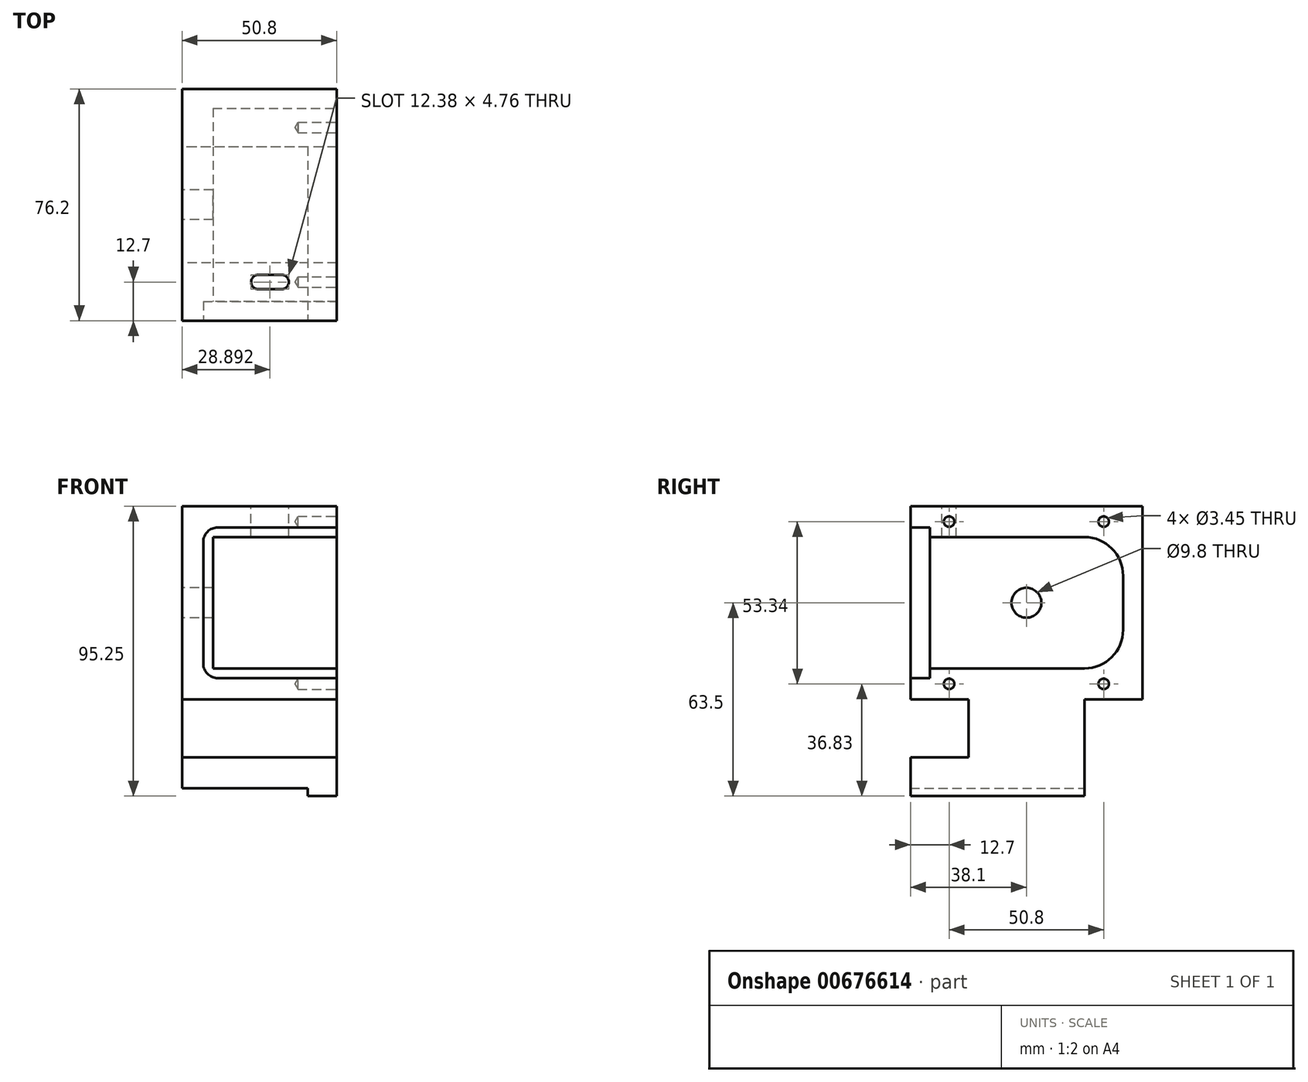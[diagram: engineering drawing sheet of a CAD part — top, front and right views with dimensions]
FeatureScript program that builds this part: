
annotation { "Feature Type Name" : "Feature", "Feature Type Description" : "" }
export const myFeature = defineFeature(function(context is Context, id is Id, definition is map)
    precondition{}
    {
        {
            var Q0;
            Q0=qCreatedBy(makeId("Right.planeOp"),FACE);
            var sketch = newSketch(context, id + "F0", { "sketchPlane" : qUnion([Q0])});
            skLineSegment(sketch, "E0.bottom", {"start": v(0, 0) * mm, "end": v(76.2, 0) * mm});
            skLineSegment(sketch, "E0.top", {"start": v(0, 63.5) * mm, "end": v(76.2, 63.5) * mm});
            skLineSegment(sketch, "E0.left", {"start": v(0, 0) * mm, "end": v(0, 63.5) * mm});
            skLineSegment(sketch, "E0.right", {"start": v(76.2, 0) * mm, "end": v(76.2, 63.5) * mm});
            skLineSegment(sketch, "E1.bottom", {"start": v(19.05, 0) * mm, "end": v(57.15, 0) * mm});
            skLineSegment(sketch, "E1.top", {"start": v(19.05, -19.05) * mm, "end": v(57.15, -19.05) * mm});
            skLineSegment(sketch, "E1.left", {"start": v(19.05, 0) * mm, "end": v(19.05, -19.05) * mm});
            skLineSegment(sketch, "E1.right", {"start": v(57.15, 0) * mm, "end": v(57.15, -19.05) * mm});
            skSolve(sketch);
        }
        {
            var Q0;
            Q0=qSketchRegion(id+"F0",true);
            extrude(context, id + "F1", {"entities" : qUnion([Q0]), "depth" : 50.8 * mm});
        }
        {
            var Q0;
            Q0=makeQuery(id+"F1.opExtrude","CAP_FACE",FACE,{"disambiguationData":[OSD([sQuery(id+"F0.wireOp",EDGE,"E0.bottom"),sQuery(id+"F0.wireOp",EDGE,"E0.top"),sQuery(id+"F0.wireOp",EDGE,"E0.left"),sQuery(id+"F0.wireOp",EDGE,"E0.right"),sQuery(id+"F0.wireOp",EDGE,"E1.top"),sQuery(id+"F0.wireOp",EDGE,"E1.left"),sQuery(id+"F0.wireOp",EDGE,"E1.right")])],"isStart":true});
            var sketch = newSketch(context, id + "F2", { "sketchPlane" : qUnion([Q0])});
            skCircle(sketch, "E2", {"center": v(-38.1, 31.75) * mm, "radius": 11.22 * mm});
            skSolve(sketch);
        }
        {
            var Q0;
            Q0=sQuery(id+"F2.wireOp",VERTEX,"E2.center");
            var Q1;
            Q1=makeQuery(id+"F1.opExtrude","SWEPT_BODY",BODY,{"disambiguationData":[OSD([sQuery(id+"F0.wireOp",EDGE,"E0.bottom"),sQuery(id+"F0.wireOp",EDGE,"E0.top"),sQuery(id+"F0.wireOp",EDGE,"E0.left"),sQuery(id+"F0.wireOp",EDGE,"E0.right"),sQuery(id+"F0.wireOp",EDGE,"E1.top"),sQuery(id+"F0.wireOp",EDGE,"E1.left"),sQuery(id+"F0.wireOp",EDGE,"E1.right")])]});
            hole(context, id + "F3", {"style" : HoleStyle.SIMPLE, "endStyle" : HoleEndStyle.THROUGH, "standardTappedOrClearance" : lookupTablePath({ "standard" : "ANSI", "fit" : "Close", "size" : "3/8", "type" : "Clearance" }), "standardBlindInLast" : lookupTablePath({ "fit" : "Close", "standard" : "ANSI", "size" : "3/8", "type" : "Clearance" }), "holeDiameter" : 9.8 * mm, "isTappedThrough" : true, "tappedDepth" : 3.96 * mm, "tapClearance" : 3, "locations" : qUnion([Q0]), "scope" : qUnion([Q1])});
        }
        {
            var Q0;
            Q0=makeQuery(id+"F1.opExtrude","SWEPT_FACE",FACE,{"disambiguationData":[OSD([sQuery(id+"F0.wireOp",EDGE,"E1.top")])]});
            var sketch = newSketch(context, id + "F4", { "sketchPlane" : qUnion([Q0])});
            skLineSegment(sketch, "E3.0", {"start": v(50.8, -76.2) * mm, "end": v(0, -76.2) * mm});
            skLineSegment(sketch, "E4.0", {"start": v(50.8, -57.15) * mm, "end": v(50.8, -76.2) * mm});
            skLineSegment(sketch, "E5.0", {"start": v(50.8, -19.05) * mm, "end": v(50.8, -57.15) * mm});
            skLineSegment(sketch, "E6.0", {"start": v(50.8, 0) * mm, "end": v(50.8, -19.05) * mm});
            skLineSegment(sketch, "E7.bottom", {"start": v(0, 0) * mm, "end": v(50.8, 0) * mm});
            skLineSegment(sketch, "E7.top", {"start": v(0, -76.2) * mm, "end": v(50.8, -76.2) * mm});
            skLineSegment(sketch, "E7.left", {"start": v(0, 0) * mm, "end": v(0, -76.2) * mm});
            skLineSegment(sketch, "E7.right", {"start": v(50.8, 0) * mm, "end": v(50.8, -76.2) * mm});
            skSolve(sketch);
        }
        {
            var Q0;
            {var subQ0=sQuery(id+"F4.wireOp",EDGE,"E7.bottom");Q0=makeQuery(id+"F4.imprint","IMPRINT",FACE,{"disambiguationData":[TD([[makeQuery(id+"F4.imprint","IMPRINT",EDGE,{"derivedFrom":subQ0}),-1.0]])]});}
            var Q1;
            {var subQ0=sQuery(id+"F4.wireOp",EDGE,"E7.top");Q1=makeQuery(id+"F4.imprint","IMPRINT",FACE,{"disambiguationData":[TD([[makeQuery(id+"F4.imprint","IMPRINT",EDGE,{"derivedFrom":subQ0}),1.0]])]});}
            var Q2;
            {var subQ0=sQuery(id+"F0.wireOp",EDGE,"E1.top");var subQ3=makeQuery(id+"F1.opExtrude","SWEPT_EDGE",EDGE,{"disambiguationData":[OSD([subQ0,sQuery(id+"F0.wireOp",EDGE,"E1.left")])]});Q2=makeQuery(id+"F4.imprint","IMPRINT",FACE,{"disambiguationData":[TD([[makeQuery(id+"F4.imprint","IMPRINT",EDGE,{"derivedFrom":subQ3}),1.0]])]});}
            extrude(context, id + "F5", {"entities" : qUnion([Q0, Q1, Q2]), "operationType" : NewBodyOperationType.ADD, "depth" : 12.7 * mm});
        }
        {
            var Q0;
            Q0=makeQuery(id+"F1.opExtrude","SWEPT_FACE",FACE,{"disambiguationData":[OSD([sQuery(id+"F0.wireOp",EDGE,"E0.left")])]});
            var sketch = newSketch(context, id + "F6", { "sketchPlane" : qUnion([Q0])});
            skSolve(sketch);
        }
        {
            var Q0;
            {var subQ0=sQuery(id+"F0.wireOp",EDGE,"E0.left");Q0=makeQuery(id+"F6.imprint","IMPRINT",FACE,{"disambiguationData":[TD([[makeQuery(id+"F6.imprint","IMPRINT",EDGE,{"derivedFrom":makeQuery(id+"F1.opExtrude","CAP_EDGE",EDGE,{"disambiguationData":[OSD([subQ0])],"isStart":true})}),-1.0]])]});}
            var sketch = newSketch(context, id + "F7", { "sketchPlane" : qUnion([Q0])});
            skLineSegment(sketch, "E8.0.0", {"start": v(0, 63.5) * mm, "end": v(0, 0) * mm});
            skLineSegment(sketch, "E8.0.1", {"start": v(0, 0) * mm, "end": v(50.8, 0) * mm});
            skLineSegment(sketch, "E8.0.2", {"start": v(50.8, 0) * mm, "end": v(50.8, 63.5) * mm});
            skLineSegment(sketch, "E8.0.3", {"start": v(50.8, 63.5) * mm, "end": v(0, 63.5) * mm});
            skLineSegment(sketch, "E9.bottom", {"start": v(10.16, 53.34) * mm, "end": v(50.8, 53.34) * mm});
            skLineSegment(sketch, "E9.top", {"start": v(10.16, 10.16) * mm, "end": v(50.8, 10.16) * mm});
            skLineSegment(sketch, "E9.left", {"start": v(10.16, 53.34) * mm, "end": v(10.16, 10.16) * mm});
            skLineSegment(sketch, "E9.right", {"start": v(50.8, 53.34) * mm, "end": v(50.8, 10.16) * mm});
            skSolve(sketch);
        }
        {
            var Q0;
            Q0=makeQuery(id+"F7.imprint","IMPRINT",FACE,{"disambiguationData":[TD([[makeQuery(id+"F7.imprint","IMPRINT",EDGE,{"derivedFrom":sQuery(id+"F7.wireOp",EDGE,"E9.bottom")}),-1.0]])]});
            extrude(context, id + "F8", {"entities" : qUnion([Q0]), "operationType" : NewBodyOperationType.REMOVE, "oppositeDirection" : true, "depth" : 69.85 * mm});
        }
        {
            var Q0;
            {var subQ0=sQuery(id+"F0.wireOp",EDGE,"E0.left");Q0=makeQuery(id+"F6.imprint","IMPRINT",FACE,{"disambiguationData":[TD([[makeQuery(id+"F6.imprint","IMPRINT",EDGE,{"derivedFrom":makeQuery(id+"F1.opExtrude","CAP_EDGE",EDGE,{"disambiguationData":[OSD([subQ0])],"isStart":true})}),-1.0]])]});}
            var sketch = newSketch(context, id + "F9", { "sketchPlane" : qUnion([Q0])});
            skLineSegment(sketch, "E10.0.0", {"start": v(0, 63.5) * mm, "end": v(0, 0) * mm});
            skLineSegment(sketch, "E10.0.1", {"start": v(0, 0) * mm, "end": v(50.8, 0) * mm});
            skLineSegment(sketch, "E10.0.2", {"start": v(50.8, 0) * mm, "end": v(50.8, 63.5) * mm});
            skLineSegment(sketch, "E10.0.3", {"start": v(50.8, 63.5) * mm, "end": v(0, 63.5) * mm});
            skLineSegment(sketch, "E11.0", {"start": v(10.16, 53.34) * mm, "end": v(50.8, 53.34) * mm});
            skLineSegment(sketch, "E12.0", {"start": v(10.16, 53.34) * mm, "end": v(10.16, 10.16) * mm});
            skLineSegment(sketch, "E13.0", {"start": v(10.16, 10.16) * mm, "end": v(50.8, 10.16) * mm});
            skLineSegment(sketch, "E14.bottom", {"start": v(6.98, 56.51) * mm, "end": v(50.8, 56.51) * mm});
            skLineSegment(sketch, "E14.top", {"start": v(6.99, 6.99) * mm, "end": v(50.8, 6.99) * mm});
            skLineSegment(sketch, "E14.left", {"start": v(6.99, 56.51) * mm, "end": v(6.99, 6.99) * mm});
            skLineSegment(sketch, "E14.right", {"start": v(50.8, 56.51) * mm, "end": v(50.8, 6.99) * mm});
            skSolve(sketch);
        }
        {
            var Q0;
            {var subQ0=sQuery(id+"F9.wireOp",EDGE,"E11.0");Q0=makeQuery(id+"F9.imprint","IMPRINT",FACE,{"disambiguationData":[TD([[makeQuery(id+"F9.imprint","IMPRINT",EDGE,{"derivedFrom":subQ0}),-1.0]])]});}
            var Q1;
            {var subQ2=sQuery(id+"F9.wireOp",EDGE,"E11.0");Q1=makeQuery(id+"F9.imprint","IMPRINT",FACE,{"disambiguationData":[TD([[makeQuery(id+"F9.imprint","IMPRINT",EDGE,{"derivedFrom":subQ2}),1.0]])]});}
            extrude(context, id + "F10", {"entities" : qUnion([Q0, Q1]), "operationType" : NewBodyOperationType.REMOVE, "oppositeDirection" : true, "depth" : 6.35 * mm});
        }
        {
            var Q0;
            Q0=makeQuery(id+"F5.boolean.opBoolean","MERGE",FACE,{"derivedFrom":[makeQuery(id+"F1.opExtrude","CAP_FACE",FACE,{"disambiguationData":[OSD([sQuery(id+"F0.wireOp",EDGE,"E0.bottom"),sQuery(id+"F0.wireOp",EDGE,"E0.top"),sQuery(id+"F0.wireOp",EDGE,"E0.left"),sQuery(id+"F0.wireOp",EDGE,"E0.right"),sQuery(id+"F0.wireOp",EDGE,"E1.top"),sQuery(id+"F0.wireOp",EDGE,"E1.left"),sQuery(id+"F0.wireOp",EDGE,"E1.right")])],"isStart":false}),makeQuery(id+"F5.opExtrude","SWEPT_FACE",FACE,{"disambiguationData":[OSD([sQuery(id+"F4.wireOp",EDGE,"E7.right")])]})]});
            var sketch = newSketch(context, id + "F11", { "sketchPlane" : qUnion([Q0])});
            skLineSegment(sketch, "E15.bottom", {"start": v(0, -19.05) * mm, "end": v(76.2, -19.05) * mm});
            skLineSegment(sketch, "E15.top", {"start": v(0, -31.75) * mm, "end": v(76.2, -31.75) * mm});
            skLineSegment(sketch, "E15.left", {"start": v(0, -19.05) * mm, "end": v(0, -31.75) * mm});
            skLineSegment(sketch, "E15.right", {"start": v(76.2, -19.05) * mm, "end": v(76.2, -31.75) * mm});
            skSolve(sketch);
        }
        {
            var Q0;
            Q0=makeQuery(id+"F11.imprint","IMPRINT",FACE,{"disambiguationData":[TD([[makeQuery(id+"F11.imprint","IMPRINT",EDGE,{"derivedFrom":sQuery(id+"F11.wireOp",EDGE,"E15.top")}),1.0]])]});
            extrude(context, id + "F12", {"entities" : qUnion([Q0]), "operationType" : NewBodyOperationType.REMOVE, "oppositeDirection" : true, "depth" : 9.52 * mm});
        }
        {
            var Q0;
            Q0=makeQuery(id+"F5.boolean.opBoolean","MERGE",FACE,{"derivedFrom":[makeQuery(id+"F1.opExtrude","CAP_FACE",FACE,{"disambiguationData":[OSD([sQuery(id+"F0.wireOp",EDGE,"E0.bottom"),sQuery(id+"F0.wireOp",EDGE,"E0.top"),sQuery(id+"F0.wireOp",EDGE,"E0.left"),sQuery(id+"F0.wireOp",EDGE,"E0.right"),sQuery(id+"F0.wireOp",EDGE,"E1.top"),sQuery(id+"F0.wireOp",EDGE,"E1.left"),sQuery(id+"F0.wireOp",EDGE,"E1.right")])],"isStart":false}),makeQuery(id+"F5.opExtrude","SWEPT_FACE",FACE,{"disambiguationData":[OSD([sQuery(id+"F4.wireOp",EDGE,"E7.right")])]})]});
            var sketch = newSketch(context, id + "F13", { "sketchPlane" : qUnion([Q0])});
            skPoint(sketch, "E16", {"position": v(12.7, 58.42) * mm});
            skPoint(sketch, "E17", {"position": v(63.5, 58.42) * mm});
            skPoint(sketch, "E18", {"position": v(12.7, 5.08) * mm});
            skPoint(sketch, "E19", {"position": v(63.5, 5.08) * mm});
            skSolve(sketch);
        }
        {
            var Q0;
            Q0=sQuery(id+"F13.wireOp",VERTEX,"E16");
            var Q1;
            Q1=sQuery(id+"F13.wireOp",VERTEX,"E17");
            var Q2;
            Q2=sQuery(id+"F13.wireOp",VERTEX,"E18");
            var Q3;
            Q3=sQuery(id+"F13.wireOp",VERTEX,"E19");
            var Q4;
            Q4=makeQuery(id+"F1.opExtrude","SWEPT_BODY",BODY,{"disambiguationData":[OSD([sQuery(id+"F0.wireOp",EDGE,"E0.bottom"),sQuery(id+"F0.wireOp",EDGE,"E0.top"),sQuery(id+"F0.wireOp",EDGE,"E0.left"),sQuery(id+"F0.wireOp",EDGE,"E0.right"),sQuery(id+"F0.wireOp",EDGE,"E1.top"),sQuery(id+"F0.wireOp",EDGE,"E1.left"),sQuery(id+"F0.wireOp",EDGE,"E1.right")])]});
            hole(context, id + "F14", {"style" : HoleStyle.SIMPLE, "endStyle" : HoleEndStyle.BLIND, "standardTappedOrClearance" : lookupTablePath({ "standard" : "ANSI", "engagement" : "75%", "pitch" : "32 tpi", "size" : "#8", "type" : "Tapped" }), "standardBlindInLast" : lookupTablePath({ "standard" : "ANSI", "engagement" : "75%", "pitch" : "32 tpi", "size" : "#8", "type" : "Tapped" }), "holeDiameter" : 3.45 * mm, "showTappedDepth" : true, "holeDepth" : 12.7 * mm, "isTappedThrough" : true, "tappedDepth" : 10.32 * mm, "tapClearance" : 3, "locations" : qUnion([Q0, Q1, Q2, Q3]), "scope" : qUnion([Q4]), "majorDiameter" : 4.17 * mm});
        }
        {
            var Q0;
            Q0=makeQuery(id+"F8.boolean.opBoolean","COPY",EDGE,{"derivedFrom":makeQuery(id+"F8.opExtrude","CAP_EDGE",EDGE,{"disambiguationData":[OSD([sQuery(id+"F7.wireOp",EDGE,"E9.bottom")])],"isStart":false})});
            fillet(context, id + "F15", {"entities" : qUnion([Q0]), "radius" : 12.7 * mm, "tangentPropagation" : true, "allowEdgeOverflow" : false});
        }
        {
            var Q0;
            Q0=makeQuery(id+"F8.boolean.opBoolean","COPY",EDGE,{"derivedFrom":makeQuery(id+"F8.opExtrude","CAP_EDGE",EDGE,{"disambiguationData":[OSD([sQuery(id+"F7.wireOp",EDGE,"E9.top")])],"isStart":false})});
            fillet(context, id + "F16", {"entities" : qUnion([Q0]), "radius" : 12.7 * mm, "tangentPropagation" : true, "allowEdgeOverflow" : false});
        }
        {
            var Q0;
            Q0=makeQuery(id+"F10.boolean.opBoolean","COPY",EDGE,{"derivedFrom":makeQuery(id+"F10.opExtrude","SWEPT_EDGE",EDGE,{"disambiguationData":[OSD([sQuery(id+"F9.wireOp",EDGE,"E14.bottom"),sQuery(id+"F9.wireOp",EDGE,"E14.left")])]})});
            var Q1;
            Q1=makeQuery(id+"F10.boolean.opBoolean","COPY",EDGE,{"derivedFrom":makeQuery(id+"F10.opExtrude","SWEPT_EDGE",EDGE,{"disambiguationData":[OSD([sQuery(id+"F9.wireOp",EDGE,"E14.top"),sQuery(id+"F9.wireOp",EDGE,"E14.left")])]})});
            fillet(context, id + "F17", {"entities" : qUnion([Q0, Q1]), "radius" : 4.76 * mm, "tangentPropagation" : true, "allowEdgeOverflow" : false});
        }
        {
            var Q0;
            Q0=makeQuery(id+"F1.opExtrude","SWEPT_FACE",FACE,{"disambiguationData":[OSD([sQuery(id+"F0.wireOp",EDGE,"E0.top")])]});
            var sketch = newSketch(context, id + "F18", { "sketchPlane" : qUnion([Q0])});
            skCircle(sketch, "E20", {"center": v(25.08, 12.7) * mm, "radius": 2.38 * mm});
            skCircle(sketch, "E21", {"center": v(32.7, 12.7) * mm, "radius": 2.38 * mm});
            skLineSegment(sketch, "E22", {"start": v(25.08, 15.08) * mm, "end": v(32.7, 15.08) * mm});
            skLineSegment(sketch, "E23", {"start": v(25.08, 10.32) * mm, "end": v(32.7, 10.32) * mm});
            skPoint(sketch, "E24", {"position": v(28.9, 12.7) * mm});
            skSolve(sketch);
        }
        {
            var Q0;
            {var subQ0=sQuery(id+"F18.wireOp",EDGE,"E22");Q0=makeQuery(id+"F18.imprint","IMPRINT",FACE,{"disambiguationData":[TD([[makeQuery(id+"F18.imprint","IMPRINT",EDGE,{"derivedFrom":subQ0}),-1.0]])]});}
            var Q1;
            {var subQ0=sQuery(id+"F18.wireOp",EDGE,"E21");var subQ1=makeQuery(id+"F18.imprint","INTERSECT",VERTEX,{"derivedFrom":[subQ0,sQuery(id+"F18.wireOp",EDGE,"E22")]});Q1=makeQuery(id+"F18.imprint","IMPRINT",FACE,{"disambiguationData":[TD([[makeQuery(id+"F18.imprint","IMPRINT",EDGE,{"disambiguationData":[TD([[subQ1,-1.0]])],"derivedFrom":subQ0}),1.0]])]});}
            var Q2;
            {var subQ0=sQuery(id+"F18.wireOp",EDGE,"E20");var subQ1=makeQuery(id+"F18.imprint","INTERSECT",VERTEX,{"derivedFrom":[subQ0,sQuery(id+"F18.wireOp",EDGE,"E22")]});Q2=makeQuery(id+"F18.imprint","IMPRINT",FACE,{"disambiguationData":[TD([[makeQuery(id+"F18.imprint","IMPRINT",EDGE,{"disambiguationData":[TD([[subQ1,-1.0]])],"derivedFrom":subQ0}),1.0]])]});}
            extrude(context, id + "F19", {"entities" : qUnion([Q0, Q1, Q2]), "operationType" : NewBodyOperationType.REMOVE, "oppositeDirection" : true, "depth" : 25.4 * mm});
        }
        {
            var Q0;
            Q0=makeQuery(id+"F5.opExtrude","CAP_FACE",FACE,{"disambiguationData":[OSD([sQuery(id+"F4.wireOp",EDGE,"E7.bottom"),sQuery(id+"F4.wireOp",EDGE,"E7.top"),sQuery(id+"F4.wireOp",EDGE,"E7.left"),sQuery(id+"F4.wireOp",EDGE,"E7.right")])],"isStart":false});
            var sketch = newSketch(context, id + "F20", { "sketchPlane" : qUnion([Q0])});
            skLineSegment(sketch, "E25.0.0", {"start": v(41.28, -76.2) * mm, "end": v(41.28, 0) * mm});
            skLineSegment(sketch, "E25.0.1", {"start": v(41.28, 0) * mm, "end": v(0, 0) * mm});
            skLineSegment(sketch, "E25.0.2", {"start": v(0, 0) * mm, "end": v(0, -76.2) * mm});
            skLineSegment(sketch, "E25.0.3", {"start": v(0, -76.2) * mm, "end": v(41.28, -76.2) * mm});
            skSolve(sketch);
        }
        {
            var Q0;
            Q0 = qSketchRegion(id + "F20", true);
            extrude(context, id + "F21", {"entities" : qUnion([Q0]), "operationType" : NewBodyOperationType.REMOVE, "oppositeDirection" : true, "depth" : 2.54 * mm, "offsetDistance" : 25.4 * mm});
        }
    });
